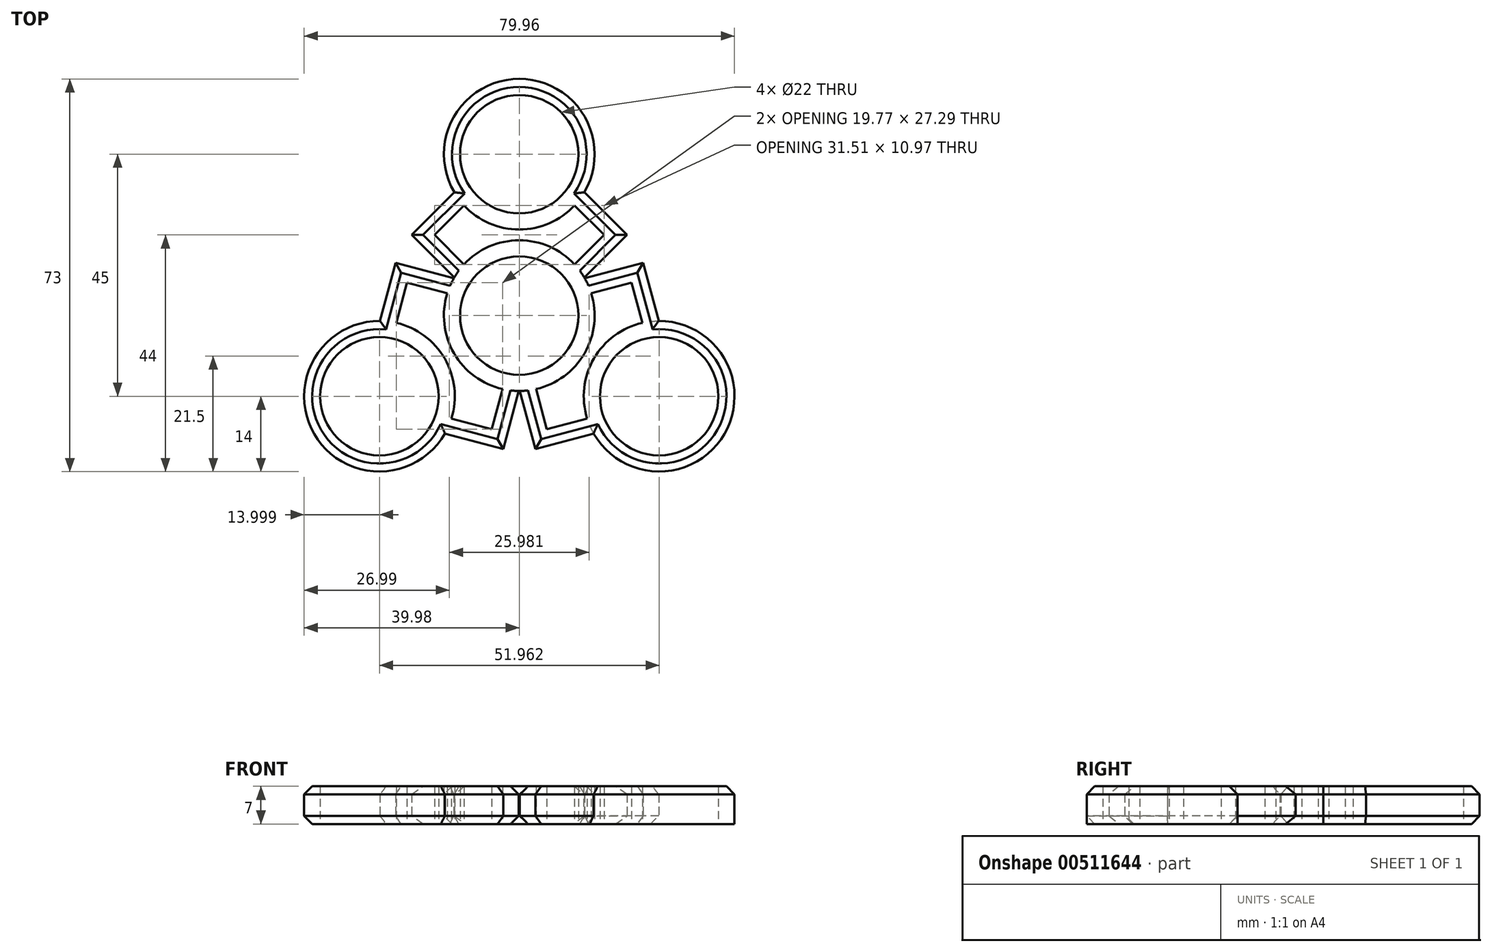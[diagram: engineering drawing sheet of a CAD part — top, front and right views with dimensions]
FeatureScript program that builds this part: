
annotation { "Feature Type Name" : "Feature", "Feature Type Description" : "" }
export const myFeature = defineFeature(function(context is Context, id is Id, definition is map)
    precondition{}
    {
        {
            var Q0;
            Q0=qCreatedBy(makeId("Top.planeOp"),FACE);
            var sketch = newSketch(context, id + "F0", { "sketchPlane" : qUnion([Q0])});
            skCircle(sketch, "E0", {"center": v(0, 0) * mm, "radius": 11 * mm});
            skCircle(sketch, "E1.0", {"center": v(0, 0) * mm, "radius": 14 * mm});
            skCircle(sketch, "E2", {"center": v(0, 30) * mm, "radius": 11 * mm});
            skCircle(sketch, "E3.0", {"center": v(0, 30) * mm, "radius": 14 * mm});
            skLineSegment(sketch, "E4", {"start": v(20, 15) * mm, "end": v(12.08, 22.92) * mm});
            skLineSegment(sketch, "E5", {"start": v(10.27, 20.49) * mm, "end": v(15.76, 15) * mm});
            skLineSegment(sketch, "E6.MirrorCS", {"start": v(10.27, 9.51) * mm, "end": v(15.76, 15) * mm});
            skLineSegment(sketch, "E7.MirrorCS", {"start": v(20, 15) * mm, "end": v(12.08, 7.08) * mm});
            skLineSegment(sketch, "E8.MirrorCS", {"start": v(-20, 15) * mm, "end": v(-12.08, 7.08) * mm});
            skLineSegment(sketch, "E9.MirrorCS", {"start": v(-10.27, 9.51) * mm, "end": v(-15.76, 15) * mm});
            skLineSegment(sketch, "E10.MirrorCS", {"start": v(-10.27, 20.49) * mm, "end": v(-15.76, 15) * mm});
            skLineSegment(sketch, "E11.MirrorCS", {"start": v(-20, 15) * mm, "end": v(-12.08, 22.92) * mm});
            skCircle(sketch, "E12.1.0", {"center": v(-25.98, -15) * mm, "radius": 11 * mm});
            skCircle(sketch, "E12.1.1", {"center": v(-25.98, -15) * mm, "radius": 14 * mm});
            skLineSegment(sketch, "E12.1.2", {"start": v(-22.88, -1.35) * mm, "end": v(-20.87, 6.15) * mm});
            skLineSegment(sketch, "E12.1.3", {"start": v(-23, 9.82) * mm, "end": v(-25.89, -1) * mm});
            skLineSegment(sketch, "E12.1.4", {"start": v(-23, 9.82) * mm, "end": v(-12.17, 6.92) * mm});
            skLineSegment(sketch, "E12.1.5", {"start": v(-13.37, 4.14) * mm, "end": v(-20.87, 6.15) * mm});
            skLineSegment(sketch, "E12.1.6", {"start": v(-3, -24.82) * mm, "end": v(-0.1, -14) * mm});
            skLineSegment(sketch, "E12.1.7", {"start": v(-3.1, -13.65) * mm, "end": v(-5.11, -21.15) * mm});
            skLineSegment(sketch, "E12.1.8", {"start": v(-12.6, -19.14) * mm, "end": v(-5.11, -21.15) * mm});
            skLineSegment(sketch, "E12.1.9", {"start": v(-3, -24.82) * mm, "end": v(-13.81, -21.92) * mm});
            skCircle(sketch, "E12.2.0", {"center": v(25.98, -15) * mm, "radius": 11 * mm});
            skCircle(sketch, "E12.2.1", {"center": v(25.98, -15) * mm, "radius": 14 * mm});
            skLineSegment(sketch, "E12.2.2", {"start": v(12.6, -19.14) * mm, "end": v(5.11, -21.15) * mm});
            skLineSegment(sketch, "E12.2.3", {"start": v(3, -24.82) * mm, "end": v(13.81, -21.92) * mm});
            skLineSegment(sketch, "E12.2.4", {"start": v(3, -24.82) * mm, "end": v(0.1, -14) * mm});
            skLineSegment(sketch, "E12.2.5", {"start": v(3.1, -13.65) * mm, "end": v(5.11, -21.15) * mm});
            skLineSegment(sketch, "E12.2.6", {"start": v(23, 9.82) * mm, "end": v(12.17, 6.92) * mm});
            skLineSegment(sketch, "E12.2.7", {"start": v(13.37, 4.14) * mm, "end": v(20.87, 6.15) * mm});
            skLineSegment(sketch, "E12.2.8", {"start": v(22.88, -1.35) * mm, "end": v(20.87, 6.15) * mm});
            skLineSegment(sketch, "E12.2.9", {"start": v(23, 9.82) * mm, "end": v(25.89, -1) * mm});
            skSolve(sketch);
        }
        {
            var Q0;
            {var subQ1=sQuery(id+"F0.wireOp",EDGE,"E4");Q0=makeQuery(id+"F0.imprint","IMPRINT",FACE,{"disambiguationData":[TD([[makeQuery(id+"F0.imprint","IMPRINT",EDGE,{"derivedFrom":subQ1}),1.0]])]});}
            var Q1;
            Q1=makeQuery(id+"F0.imprint","IMPRINT",FACE,{"disambiguationData":[TD([[makeQuery(id+"F0.imprint","IMPRINT",EDGE,{"derivedFrom":sQuery(id+"F0.wireOp",EDGE,"E2")}),-1.0]])]});
            var Q2;
            {var subQ1=sQuery(id+"F0.wireOp",EDGE,"E8.MirrorCS");Q2=makeQuery(id+"F0.imprint","IMPRINT",FACE,{"disambiguationData":[TD([[makeQuery(id+"F0.imprint","IMPRINT",EDGE,{"derivedFrom":subQ1}),1.0]])]});}
            var Q3;
            {var subQ0=sQuery(id+"F0.wireOp",EDGE,"E12.1.2");Q3=makeQuery(id+"F0.imprint","IMPRINT",FACE,{"disambiguationData":[TD([[makeQuery(id+"F0.imprint","IMPRINT",EDGE,{"derivedFrom":subQ0}),1.0]])]});}
            var Q4;
            Q4=makeQuery(id+"F0.imprint","IMPRINT",FACE,{"disambiguationData":[TD([[makeQuery(id+"F0.imprint","IMPRINT",EDGE,{"derivedFrom":sQuery(id+"F0.wireOp",EDGE,"E0")}),-1.0]])]});
            var Q5;
            Q5=makeQuery(id+"F0.imprint","IMPRINT",FACE,{"disambiguationData":[TD([[makeQuery(id+"F0.imprint","IMPRINT",EDGE,{"derivedFrom":sQuery(id+"F0.wireOp",EDGE,"E12.1.0")}),-1.0]])]});
            var Q6;
            {var subQ1=sQuery(id+"F0.wireOp",EDGE,"E12.1.6");Q6=makeQuery(id+"F0.imprint","IMPRINT",FACE,{"disambiguationData":[TD([[makeQuery(id+"F0.imprint","IMPRINT",EDGE,{"derivedFrom":subQ1}),1.0]])]});}
            var Q7;
            {var subQ1=sQuery(id+"F0.wireOp",EDGE,"E12.2.2");Q7=makeQuery(id+"F0.imprint","IMPRINT",FACE,{"disambiguationData":[TD([[makeQuery(id+"F0.imprint","IMPRINT",EDGE,{"derivedFrom":subQ1}),1.0]])]});}
            var Q8;
            {var subQ1=sQuery(id+"F0.wireOp",EDGE,"E12.2.6");Q8=makeQuery(id+"F0.imprint","IMPRINT",FACE,{"disambiguationData":[TD([[makeQuery(id+"F0.imprint","IMPRINT",EDGE,{"derivedFrom":subQ1}),1.0]])]});}
            var Q9;
            Q9=makeQuery(id+"F0.imprint","IMPRINT",FACE,{"disambiguationData":[TD([[makeQuery(id+"F0.imprint","IMPRINT",EDGE,{"derivedFrom":sQuery(id+"F0.wireOp",EDGE,"E12.2.0")}),-1.0]])]});
            extrude(context, id + "F1", {"entities" : qUnion([Q0, Q1, Q2, Q3, Q4, Q5, Q6, Q7, Q8, Q9]), "depth" : 7 * mm});
        }
        {
            var Q0;
            {var subQ0=sQuery(id+"F0.wireOp",EDGE,"E3.0");Q0=makeQuery(id+"F1.opExtrude","CAP_EDGE",EDGE,{"disambiguationData":[OSD([subQ0]),TDD([makeQuery(id+"F0.imprint","IMPRINT",EDGE,{"disambiguationData":[TD([[makeQuery(id+"F0.imprint","INTERSECT",VERTEX,{"derivedFrom":[subQ0,sQuery(id+"F0.wireOp",EDGE,"E4")]}),-1.0]])],"derivedFrom":subQ0})])],"isStart":false});}
            var Q1;
            Q1=makeQuery(id+"F1.opExtrude","CAP_EDGE",EDGE,{"disambiguationData":[OSD([sQuery(id+"F0.wireOp",EDGE,"E11.MirrorCS")])],"isStart":false});
            var Q2;
            Q2=makeQuery(id+"F1.opExtrude","CAP_EDGE",EDGE,{"disambiguationData":[OSD([sQuery(id+"F0.wireOp",EDGE,"E8.MirrorCS")])],"isStart":false});
            var Q3;
            Q3=makeQuery(id+"F1.opExtrude","CAP_EDGE",EDGE,{"disambiguationData":[OSD([sQuery(id+"F0.wireOp",EDGE,"E12.1.4")])],"isStart":false});
            var Q4;
            Q4=makeQuery(id+"F1.opExtrude","CAP_EDGE",EDGE,{"disambiguationData":[OSD([sQuery(id+"F0.wireOp",EDGE,"E12.1.3")])],"isStart":false});
            var Q5;
            {var subQ0=sQuery(id+"F0.wireOp",EDGE,"E12.1.1");Q5=makeQuery(id+"F1.opExtrude","CAP_EDGE",EDGE,{"disambiguationData":[OSD([subQ0]),TDD([makeQuery(id+"F0.imprint","IMPRINT",EDGE,{"disambiguationData":[TD([[makeQuery(id+"F0.imprint","INTERSECT",VERTEX,{"derivedFrom":[subQ0,sQuery(id+"F0.wireOp",EDGE,"E12.1.3")]}),-1.0]])],"derivedFrom":subQ0})])],"isStart":false});}
            var Q6;
            Q6=makeQuery(id+"F1.opExtrude","CAP_EDGE",EDGE,{"disambiguationData":[OSD([sQuery(id+"F0.wireOp",EDGE,"E12.1.9")])],"isStart":false});
            var Q7;
            Q7=makeQuery(id+"F1.opExtrude","CAP_EDGE",EDGE,{"disambiguationData":[OSD([sQuery(id+"F0.wireOp",EDGE,"E12.1.6")])],"isStart":false});
            var Q8;
            Q8=makeQuery(id+"F1.opExtrude","CAP_EDGE",EDGE,{"disambiguationData":[OSD([sQuery(id+"F0.wireOp",EDGE,"E12.2.4")])],"isStart":false});
            var Q9;
            Q9=makeQuery(id+"F1.opExtrude","CAP_EDGE",EDGE,{"disambiguationData":[OSD([sQuery(id+"F0.wireOp",EDGE,"E12.2.3")])],"isStart":false});
            var Q10;
            {var subQ0=sQuery(id+"F0.wireOp",EDGE,"E12.2.1");Q10=makeQuery(id+"F1.opExtrude","CAP_EDGE",EDGE,{"disambiguationData":[OSD([subQ0]),TDD([makeQuery(id+"F0.imprint","IMPRINT",EDGE,{"disambiguationData":[TD([[makeQuery(id+"F0.imprint","INTERSECT",VERTEX,{"derivedFrom":[subQ0,sQuery(id+"F0.wireOp",EDGE,"E12.2.3")]}),-1.0]])],"derivedFrom":subQ0})])],"isStart":false});}
            var Q11;
            Q11=makeQuery(id+"F1.opExtrude","CAP_EDGE",EDGE,{"disambiguationData":[OSD([sQuery(id+"F0.wireOp",EDGE,"E12.2.9")])],"isStart":false});
            var Q12;
            Q12=makeQuery(id+"F1.opExtrude","CAP_EDGE",EDGE,{"disambiguationData":[OSD([sQuery(id+"F0.wireOp",EDGE,"E12.2.6")])],"isStart":false});
            var Q13;
            Q13=makeQuery(id+"F1.opExtrude","CAP_EDGE",EDGE,{"disambiguationData":[OSD([sQuery(id+"F0.wireOp",EDGE,"E7.MirrorCS")])],"isStart":false});
            var Q14;
            Q14=makeQuery(id+"F1.opExtrude","CAP_EDGE",EDGE,{"disambiguationData":[OSD([sQuery(id+"F0.wireOp",EDGE,"E4")])],"isStart":false});
            var Q15;
            Q15=makeQuery(id+"F1.opExtrude","CAP_EDGE",EDGE,{"disambiguationData":[OSD([sQuery(id+"F0.wireOp",EDGE,"E12.2.3")])],"isStart":true});
            var Q16;
            Q16=makeQuery(id+"F1.opExtrude","CAP_EDGE",EDGE,{"disambiguationData":[OSD([sQuery(id+"F0.wireOp",EDGE,"E12.2.9")])],"isStart":true});
            var Q17;
            Q17=makeQuery(id+"F1.opExtrude","CAP_EDGE",EDGE,{"disambiguationData":[OSD([sQuery(id+"F0.wireOp",EDGE,"E12.2.6")])],"isStart":true});
            var Q18;
            Q18=makeQuery(id+"F1.opExtrude","CAP_EDGE",EDGE,{"disambiguationData":[OSD([sQuery(id+"F0.wireOp",EDGE,"E7.MirrorCS")])],"isStart":true});
            var Q19;
            Q19=makeQuery(id+"F1.opExtrude","CAP_EDGE",EDGE,{"disambiguationData":[OSD([sQuery(id+"F0.wireOp",EDGE,"E4")])],"isStart":true});
            var Q20;
            {var subQ0=sQuery(id+"F0.wireOp",EDGE,"E3.0");Q20=makeQuery(id+"F1.opExtrude","CAP_EDGE",EDGE,{"disambiguationData":[OSD([subQ0]),TDD([makeQuery(id+"F0.imprint","IMPRINT",EDGE,{"disambiguationData":[TD([[makeQuery(id+"F0.imprint","INTERSECT",VERTEX,{"derivedFrom":[subQ0,sQuery(id+"F0.wireOp",EDGE,"E4")]}),-1.0]])],"derivedFrom":subQ0})])],"isStart":true});}
            var Q21;
            Q21=makeQuery(id+"F1.opExtrude","CAP_EDGE",EDGE,{"disambiguationData":[OSD([sQuery(id+"F0.wireOp",EDGE,"E11.MirrorCS")])],"isStart":true});
            var Q22;
            Q22=makeQuery(id+"F1.opExtrude","CAP_EDGE",EDGE,{"disambiguationData":[OSD([sQuery(id+"F0.wireOp",EDGE,"E8.MirrorCS")])],"isStart":true});
            var Q23;
            Q23=makeQuery(id+"F1.opExtrude","CAP_EDGE",EDGE,{"disambiguationData":[OSD([sQuery(id+"F0.wireOp",EDGE,"E12.1.4")])],"isStart":true});
            var Q24;
            Q24=makeQuery(id+"F1.opExtrude","CAP_EDGE",EDGE,{"disambiguationData":[OSD([sQuery(id+"F0.wireOp",EDGE,"E12.1.3")])],"isStart":true});
            var Q25;
            {var subQ0=sQuery(id+"F0.wireOp",EDGE,"E12.1.1");Q25=makeQuery(id+"F1.opExtrude","CAP_EDGE",EDGE,{"disambiguationData":[OSD([subQ0]),TDD([makeQuery(id+"F0.imprint","IMPRINT",EDGE,{"disambiguationData":[TD([[makeQuery(id+"F0.imprint","INTERSECT",VERTEX,{"derivedFrom":[subQ0,sQuery(id+"F0.wireOp",EDGE,"E12.1.3")]}),-1.0]])],"derivedFrom":subQ0})])],"isStart":true});}
            var Q26;
            Q26=makeQuery(id+"F1.opExtrude","CAP_EDGE",EDGE,{"disambiguationData":[OSD([sQuery(id+"F0.wireOp",EDGE,"E12.1.9")])],"isStart":true});
            var Q27;
            Q27=makeQuery(id+"F1.opExtrude","CAP_EDGE",EDGE,{"disambiguationData":[OSD([sQuery(id+"F0.wireOp",EDGE,"E12.1.6")])],"isStart":true});
            var Q28;
            Q28=makeQuery(id+"F1.opExtrude","CAP_EDGE",EDGE,{"disambiguationData":[OSD([sQuery(id+"F0.wireOp",EDGE,"E12.2.4")])],"isStart":true});
            chamfer(context, id + "F2", {"entities" : qUnion([Q0, Q1, Q2, Q3, Q4, Q5, Q6, Q7, Q8, Q9, Q10, Q11, Q12, Q13, Q14, Q15, Q16, Q17, Q18, Q19, Q20, Q21, Q22, Q23, Q24, Q25, Q26, Q27, Q28]), "width" : 1.5 * mm, "tangentPropagation" : true});
        }
    });
